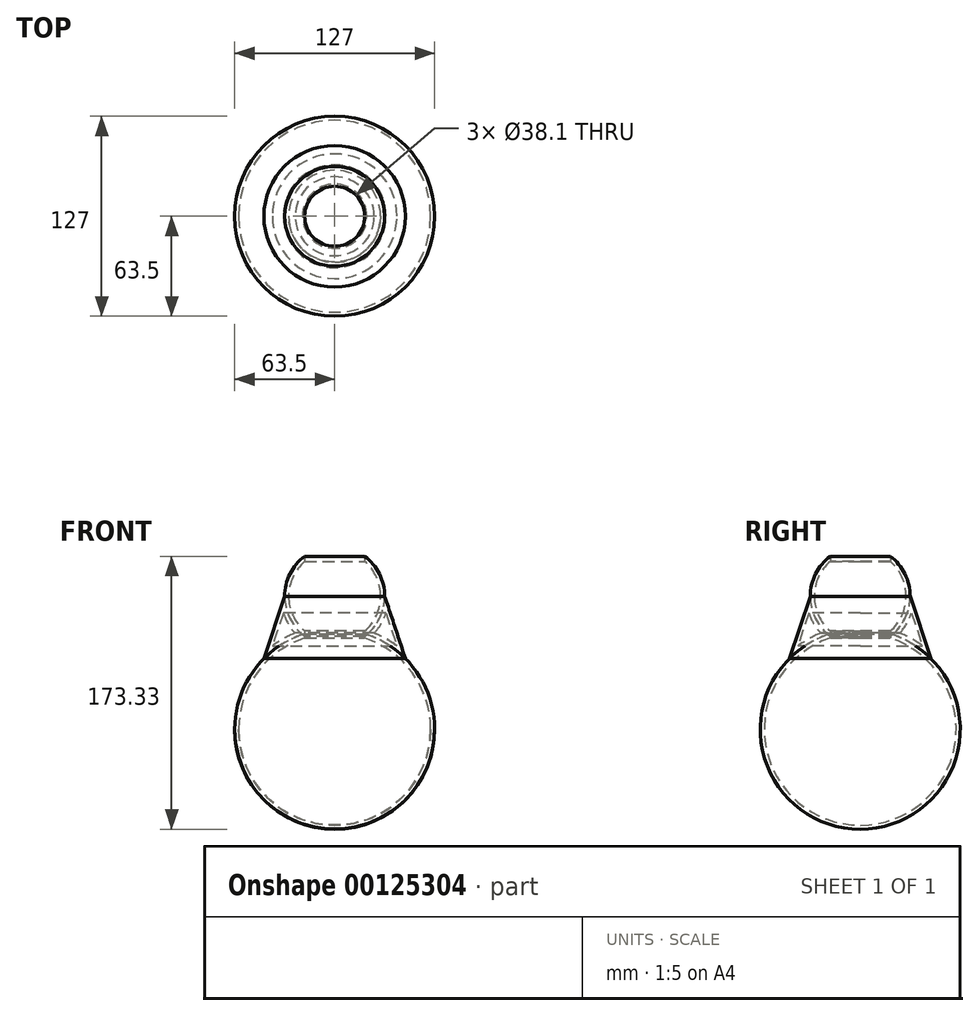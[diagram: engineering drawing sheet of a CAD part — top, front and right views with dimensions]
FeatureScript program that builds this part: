
annotation { "Feature Type Name" : "Feature", "Feature Type Description" : "" }
export const myFeature = defineFeature(function(context is Context, id is Id, definition is map)
    precondition{}
    {
        {
            var Q0;
            Q0=qCreatedBy(makeId("Front.planeOp"),FACE);
            var sketch = newSketch(context, id + "F0", { "sketchPlane" : qUnion([Q0])});
            skCircle(sketch, "E0", {"center": v(0, 0) * mm, "radius": 63.5 * mm});
            skLineSegment(sketch, "E1", {"start": v(-63.5, 0) * mm, "end": v(63.5, 0) * mm});
            skCircle(sketch, "E2", {"center": v(0, 84.43) * mm, "radius": 31.75 * mm});
            skLineSegment(sketch, "E3", {"start": v(0, 84.43) * mm, "end": v(-31.75, 84.43) * mm});
            skLineSegment(sketch, "E4", {"start": v(-31.75, 84.43) * mm, "end": v(31.75, 84.43) * mm});
            skLineSegment(sketch, "E5", {"start": v(-31.75, 84.43) * mm, "end": v(-44.94, 44.86) * mm});
            skLineSegment(sketch, "E6", {"start": v(31.75, 84.43) * mm, "end": v(44.94, 44.86) * mm});
            skLineSegment(sketch, "E7", {"start": v(0, 116.18) * mm, "end": v(0, 52.68) * mm});
            skSolve(sketch);
        }
        {
            var Q0;
            {var subQ0=sQuery(id+"F0.wireOp",EDGE,"E1");Q0=makeQuery(id+"F0.imprint","IMPRINT",FACE,{"disambiguationData":[TD([[makeQuery(id+"F0.imprint","IMPRINT",EDGE,{"derivedFrom":subQ0}),-1.0]])]});}
            var Q1;
            Q1=sQuery(id+"F0.wireOp",EDGE,"E1");
            revolve(context, id + "F1", {"entities" : qUnion([Q0]), "axis" : qUnion([Q1]), "revolveType" : RevolveType.FULL});
        }
        {
            var Q0;
            {var subQ1=sQuery(id+"F0.wireOp",EDGE,"E2");var subQ3=sQuery(id+"F0.wireOp",EDGE,"E7");var subQ4=makeQuery(id+"F0.imprint","INTERSECT",VERTEX,{"disambiguationData":[OD(0.0)],"derivedFrom":[subQ1,subQ3]});Q0=makeQuery(id+"F0.imprint","IMPRINT",FACE,{"disambiguationData":[TD([[makeQuery(id+"F0.imprint","IMPRINT",EDGE,{"disambiguationData":[TD([[subQ4,-1.0]])],"derivedFrom":subQ3}),1.0]])]});}
            var Q1;
            {var subQ1=sQuery(id+"F0.wireOp",EDGE,"E2");var subQ3=sQuery(id+"F0.wireOp",EDGE,"E7");var subQ4=makeQuery(id+"F0.imprint","INTERSECT",VERTEX,{"disambiguationData":[OD(0.0)],"derivedFrom":[subQ1,subQ3]});Q1=makeQuery(id+"F0.imprint","IMPRINT",FACE,{"disambiguationData":[TD([[makeQuery(id+"F0.imprint","IMPRINT",EDGE,{"disambiguationData":[TD([[subQ4,-1.0]])],"derivedFrom":subQ3}),-1.0]])]});}
            var Q2;
            Q2=sQuery(id+"F0.wireOp",EDGE,"E4");
            revolve(context, id + "F2", {"entities" : qUnion([Q0, Q1]), "axis" : qUnion([Q2]), "revolveType" : RevolveType.FULL});
        }
        {
            var Q0;
            {var subQ0=sQuery(id+"F0.wireOp",EDGE,"E6");Q0=makeQuery(id+"F0.imprint","IMPRINT",FACE,{"disambiguationData":[TD([[makeQuery(id+"F0.imprint","IMPRINT",EDGE,{"derivedFrom":subQ0}),-1.0]])]});}
            var Q1;
            Q1=sQuery(id+"F0.wireOp",EDGE,"E7");
            revolve(context, id + "F3", {"entities" : qUnion([Q0]), "axis" : qUnion([Q1]), "revolveType" : RevolveType.FULL});
        }
        {
            var Q0;
            Q0=qCreatedBy(makeId("Top.planeOp"),FACE);
            var sketch = newSketch(context, id + "F4", { "sketchPlane" : qUnion([Q0])});
            skCircle(sketch, "E8", {"center": v(0, 0) * mm, "radius": 19.05 * mm});
            skSolve(sketch);
        }
        {
            var Q0;
            Q0=makeQuery(id+"F2.opRevolve","SWEPT_FACE",FACE,{"disambiguationData":[OSD([sQuery(id+"F0.wireOp",EDGE,"E2")])]});
            var Q1;
            Q1=makeQuery(id+"F3.opRevolve","SWEPT_FACE",FACE,{"disambiguationData":[OSD([sQuery(id+"F0.wireOp",EDGE,"E6")])]});
            var Q2;
            Q2=makeQuery(id+"F1.opRevolve","SWEPT_FACE",FACE,{"disambiguationData":[OSD([sQuery(id+"F0.wireOp",EDGE,"E0")])]});
            var Q3;
            Q3=makeQuery(id+"F2.opRevolve","SWEPT_BODY",BODY,{"disambiguationData":[OSD([sQuery(id+"F0.wireOp",EDGE,"E2"),sQuery(id+"F0.wireOp",EDGE,"E4")])]});
            var Q4;
            Q4=makeQuery(id+"F3.opRevolve","SWEPT_BODY",BODY,{"disambiguationData":[OSD([sQuery(id+"F0.wireOp",EDGE,"E0"),sQuery(id+"F0.wireOp",EDGE,"E2"),sQuery(id+"F0.wireOp",EDGE,"E6")])]});
            var Q5;
            Q5=makeQuery(id+"F1.opRevolve","SWEPT_BODY",BODY,{"disambiguationData":[OSD([sQuery(id+"F0.wireOp",EDGE,"E0"),sQuery(id+"F0.wireOp",EDGE,"E1")])]});
            shell(context, id + "F5", {"isHollow" : true, "entities" : qUnion([Q0, Q1, Q2]), "parts" : qUnion([Q3, Q4, Q5]), "thickness" : 2.54 * mm});
        }
        {
            var Q0;
            Q0=makeQuery(id+"F4.imprint","IMPRINT",FACE,{"disambiguationData":[TD([[makeQuery(id+"F4.imprint","IMPRINT",EDGE,{"derivedFrom":sQuery(id+"F4.wireOp",EDGE,"E8")}),1.0]])]});
            extrude(context, id + "F6", {"entities" : qUnion([Q0]), "operationType" : NewBodyOperationType.REMOVE, "depth" : 149.7 * mm});
        }
    });
